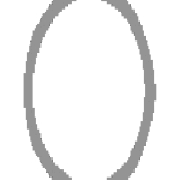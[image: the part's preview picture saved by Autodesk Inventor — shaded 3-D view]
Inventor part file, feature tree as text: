
AUTODESK INVENTOR PART (.ipt)
format: ipt  version: 2021 (Build 250183000, 183)  size: 112,128 bytes
history: native  units: in
note: dims shown in document units (in); Inventor stores cm internally (conversion verified against a paired STEP export)
features: other x4, sketch x3, plane x1
ambient origin geometry x8: Origin, YZ Plane, XZ Plane, XY Plane, X Axis, Y Axis, Z Axis, Center Point
bodies: Solid1 (feature_tree), Body (feature_tree)
feature tree (8):
  other  "Driven Length"
  other  "Frame Generator"
  other  "Start Plane"
  other  "End Plane"
  sketch  "Sketch"  dims[d2=20.0in d4=-0.0in d5=20.0in d6=0.12in d7=0.0in d8=90.0deg d9=20.0in]
  sketch  "Sketch2"  dims[d0=1.0in]
  plane  "Work Plane3"
  sketch  "Sketch3"  dims[d1=0.065in]
